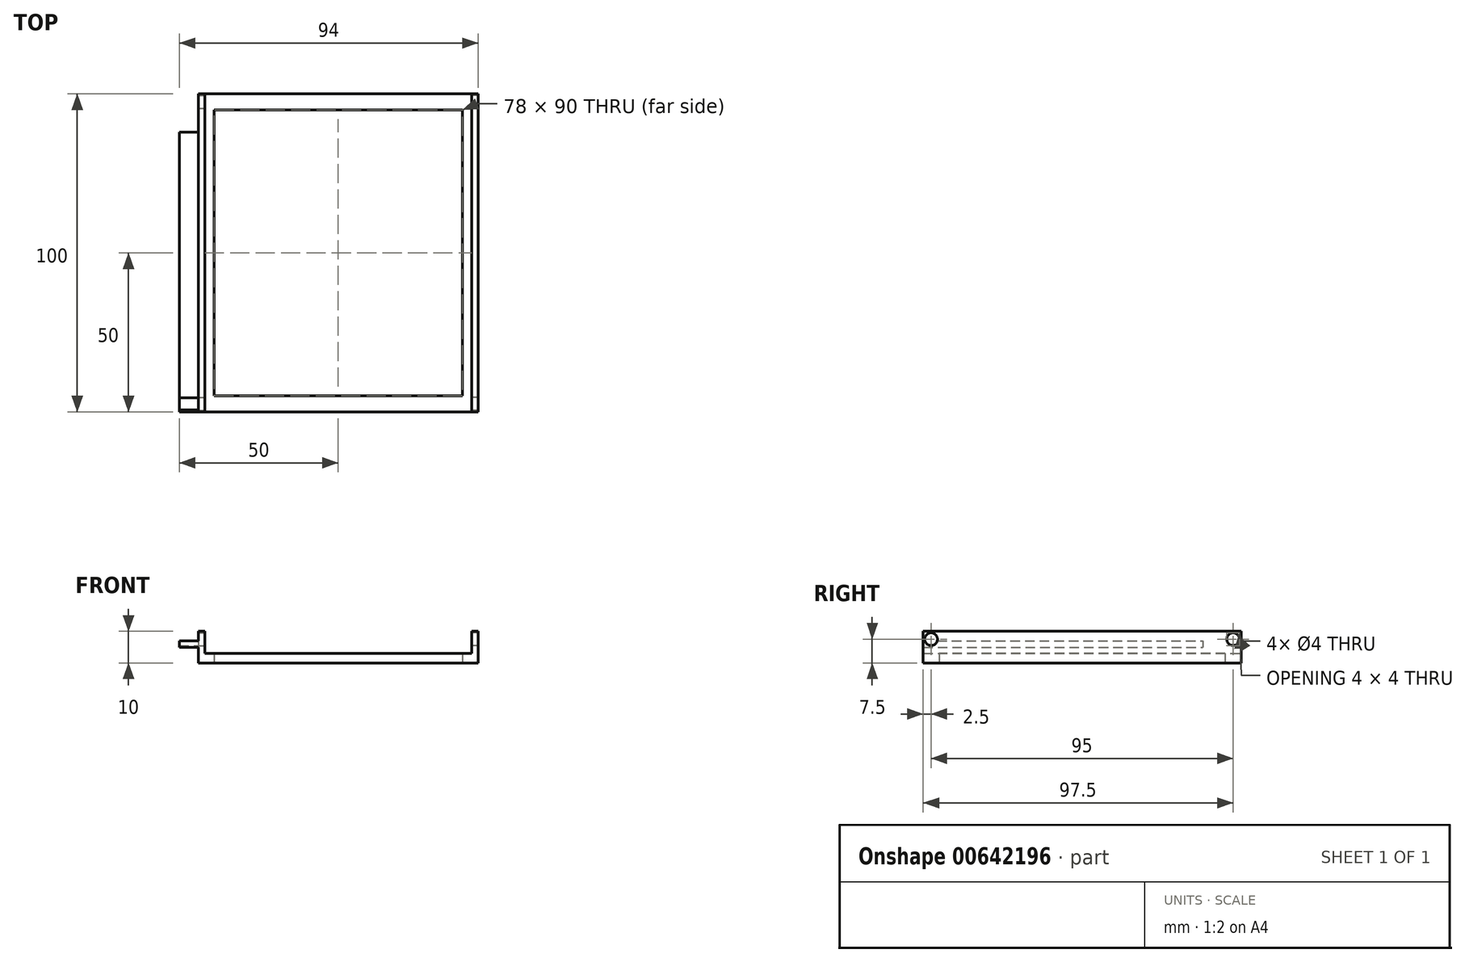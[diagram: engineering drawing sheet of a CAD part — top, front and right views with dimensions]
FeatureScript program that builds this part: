
annotation { "Feature Type Name" : "Feature", "Feature Type Description" : "" }
export const myFeature = defineFeature(function(context is Context, id is Id, definition is map)
    precondition{}
    {
        {
            var Q0;
            Q0=qCreatedBy(makeId("Front.planeOp"),FACE);
            var sketch = newSketch(context, id + "F0", { "sketchPlane" : qUnion([Q0])});
            skLineSegment(sketch, "E0", {"start": v(0, 0) * mm, "end": v(86, 0) * mm});
            skLineSegment(sketch, "E1", {"start": v(86, 0) * mm, "end": v(86, 10) * mm});
            skLineSegment(sketch, "E2", {"start": v(86, 10) * mm, "end": v(84, 10) * mm});
            skLineSegment(sketch, "E3", {"start": v(84, 10) * mm, "end": v(84, 3) * mm});
            skLineSegment(sketch, "E4", {"start": v(84, 3) * mm, "end": v(0, 3) * mm});
            skLineSegment(sketch, "E5", {"start": v(0, 3) * mm, "end": v(0, 7) * mm});
            skLineSegment(sketch, "E6", {"start": v(0, 7) * mm, "end": v(-8, 7) * mm});
            skLineSegment(sketch, "E7", {"start": v(-8, 7) * mm, "end": v(-8, 5) * mm});
            skLineSegment(sketch, "E8", {"start": v(-8, 5) * mm, "end": v(-2, 5) * mm});
            skLineSegment(sketch, "E9", {"start": v(-2, 5) * mm, "end": v(-2, 0) * mm});
            skLineSegment(sketch, "E10", {"start": v(-2, 0) * mm, "end": v(0, 0) * mm});
            skLineSegment(sketch, "E11", {"start": v(0, 7) * mm, "end": v(0, 3) * mm});
            skLineSegment(sketch, "E12", {"start": v(-2, 7) * mm, "end": v(-2, 10) * mm});
            skLineSegment(sketch, "E13", {"start": v(-2, 10) * mm, "end": v(0, 10) * mm});
            skLineSegment(sketch, "E14", {"start": v(0, 10) * mm, "end": v(0, 7) * mm});
            skSolve(sketch);
        }
        {
            var Q0;
            Q0=makeQuery(id+"F0.imprint","IMPRINT",FACE,{"disambiguationData":[TD([[makeQuery(id+"F0.imprint","IMPRINT",EDGE,{"derivedFrom":sQuery(id+"F0.wireOp",EDGE,"E0")}),1.0]])]});
            var Q1;
            {var subQ2=sQuery(id+"F0.wireOp",EDGE,"E12");Q1=makeQuery(id+"F0.imprint","IMPRINT",FACE,{"disambiguationData":[TD([[makeQuery(id+"F0.imprint","IMPRINT",EDGE,{"derivedFrom":subQ2}),-1.0]])]});}
            extrude(context, id + "F1", {"entities" : qUnion([Q0, Q1]), "depth" : 100 * mm, "offsetDistance" : 25 * mm});
        }
        {
            var Q0;
            Q0=qCreatedBy(makeId("Top.planeOp"),FACE);
            var sketch = newSketch(context, id + "F2", { "sketchPlane" : qUnion([Q0])});
            skLineSegment(sketch, "E15.bottom", {"start": v(3, -5) * mm, "end": v(81, -5) * mm});
            skLineSegment(sketch, "E15.top", {"start": v(3, -95) * mm, "end": v(81, -95) * mm});
            skLineSegment(sketch, "E15.left", {"start": v(3, -5) * mm, "end": v(3, -95) * mm});
            skLineSegment(sketch, "E15.right", {"start": v(81, -5) * mm, "end": v(81, -95) * mm});
            skSolve(sketch);
        }
        {
            var Q0;
            Q0 = qSketchRegion(id + "F2", true);
            var Q1;
            Q1 = qSketchRegion(id + "F4", true);
            var Q2;
            Q2=makeQuery(id+"F1.opExtrude","SWEPT_FACE",FACE,{"disambiguationData":[OSD([sQuery(id+"F0.wireOp",EDGE,"E6")])]});
            extrude(context, id + "F3", {"entities" : qUnion([Q0, Q1, Q2]), "operationType" : NewBodyOperationType.REMOVE, "depth" : 3 * mm, "offsetDistance" : 25 * mm});
        }
        {
            var Q0;
            Q0=qCreatedBy(makeId("Top.planeOp"),FACE);
            var sketch = newSketch(context, id + "F4", { "sketchPlane" : qUnion([Q0])});
            skLineSegment(sketch, "E16", {"start": v(-8, 0) * mm, "end": v(-8, -12) * mm});
            skLineSegment(sketch, "E17", {"start": v(-8, -12) * mm, "end": v(-2, -12) * mm});
            skLineSegment(sketch, "E18", {"start": v(-2, -12) * mm, "end": v(-2, 0) * mm});
            skLineSegment(sketch, "E19", {"start": v(-2, 0) * mm, "end": v(-8, 0) * mm});
            skLineSegment(sketch, "E20", {"start": v(-8, -100) * mm, "end": v(-8, -88) * mm});
            skLineSegment(sketch, "E21", {"start": v(-8, -88) * mm, "end": v(-2, -88) * mm});
            skLineSegment(sketch, "E22", {"start": v(-2, -88) * mm, "end": v(-2, -100) * mm});
            skSolve(sketch);
        }
        {
            var Q0;
            Q0=makeQuery(id+"F4.imprint","IMPRINT",FACE,{"disambiguationData":[TD([[makeQuery(id+"F4.imprint","IMPRINT",EDGE,{"derivedFrom":sQuery(id+"F4.wireOp",EDGE,"E16")}),1.0]])]});
            extrude(context, id + "F5", {"entities" : qUnion([Q0]), "operationType" : NewBodyOperationType.REMOVE, "depth" : 10 * mm, "offsetDistance" : 25 * mm});
        }
        {
            var Q0;
            Q0=qCreatedBy(makeId("Right.planeOp"),FACE);
            var sketch = newSketch(context, id + "F6", { "sketchPlane" : qUnion([Q0])});
            skPoint(sketch, "E23", {"position": v(-2.5, 7.5) * mm});
            skPoint(sketch, "E24", {"position": v(-97.5, 7.5) * mm});
            skSolve(sketch);
        }
        {
            var Q0;
            Q0=sQuery(id+"F6.wireOp",VERTEX,"E23");
            var Q1;
            Q1=sQuery(id+"F6.wireOp",VERTEX,"E24");
            var Q2;
            Q2=makeQuery(id+"F1.opExtrude","SWEPT_BODY",BODY,{"disambiguationData":[OSD([sQuery(id+"F0.wireOp",EDGE,"E0"),sQuery(id+"F0.wireOp",EDGE,"E1"),sQuery(id+"F0.wireOp",EDGE,"E2"),sQuery(id+"F0.wireOp",EDGE,"E3"),sQuery(id+"F0.wireOp",EDGE,"E4"),sQuery(id+"F0.wireOp",EDGE,"E6"),sQuery(id+"F0.wireOp",EDGE,"E7"),sQuery(id+"F0.wireOp",EDGE,"E8"),sQuery(id+"F0.wireOp",EDGE,"E9"),sQuery(id+"F0.wireOp",EDGE,"E10"),sQuery(id+"F0.wireOp",EDGE,"E11"),sQuery(id+"F0.wireOp",EDGE,"E12"),sQuery(id+"F0.wireOp",EDGE,"E13"),sQuery(id+"F0.wireOp",EDGE,"E14")])]});
            hole(context, id + "F7", {"style" : HoleStyle.SIMPLE, "endStyle" : HoleEndStyle.THROUGH, "holeDiameter" : 4 * mm, "majorDiameter" : 5 * mm, "isTappedThrough" : true, "tappedDepth" : 12 * mm, "tapClearance" : 3, "locations" : qUnion([Q0, Q1]), "scope" : qUnion([Q2])});
        }
        {
            var Q0;
            Q0=qCreatedBy(makeId("Right.planeOp"),FACE);
            var sketch = newSketch(context, id + "F8", { "sketchPlane" : qUnion([Q0])});
            skPoint(sketch, "E25", {"position": v(-2.5, 7.5) * mm});
            skPoint(sketch, "E26", {"position": v(-97.5, 7.5) * mm});
            skSolve(sketch);
        }
        {
            var Q0;
            Q0=sQuery(id+"F8.wireOp",VERTEX,"E25");
            var Q1;
            Q1=sQuery(id+"F8.wireOp",VERTEX,"E26");
            var Q2;
            Q2=makeQuery(id+"F1.opExtrude","SWEPT_BODY",BODY,{"disambiguationData":[OSD([sQuery(id+"F0.wireOp",EDGE,"E0"),sQuery(id+"F0.wireOp",EDGE,"E1"),sQuery(id+"F0.wireOp",EDGE,"E2"),sQuery(id+"F0.wireOp",EDGE,"E3"),sQuery(id+"F0.wireOp",EDGE,"E4"),sQuery(id+"F0.wireOp",EDGE,"E6"),sQuery(id+"F0.wireOp",EDGE,"E7"),sQuery(id+"F0.wireOp",EDGE,"E8"),sQuery(id+"F0.wireOp",EDGE,"E9"),sQuery(id+"F0.wireOp",EDGE,"E10"),sQuery(id+"F0.wireOp",EDGE,"E11"),sQuery(id+"F0.wireOp",EDGE,"E12"),sQuery(id+"F0.wireOp",EDGE,"E13"),sQuery(id+"F0.wireOp",EDGE,"E14")])]});
            hole(context, id + "F9", {"style" : HoleStyle.SIMPLE, "endStyle" : HoleEndStyle.THROUGH, "oppositeDirection" : true, "holeDiameter" : 4 * mm, "majorDiameter" : 5 * mm, "isTappedThrough" : true, "tappedDepth" : 12 * mm, "tapClearance" : 3, "locations" : qUnion([Q0, Q1]), "scope" : qUnion([Q2])});
        }
    });
